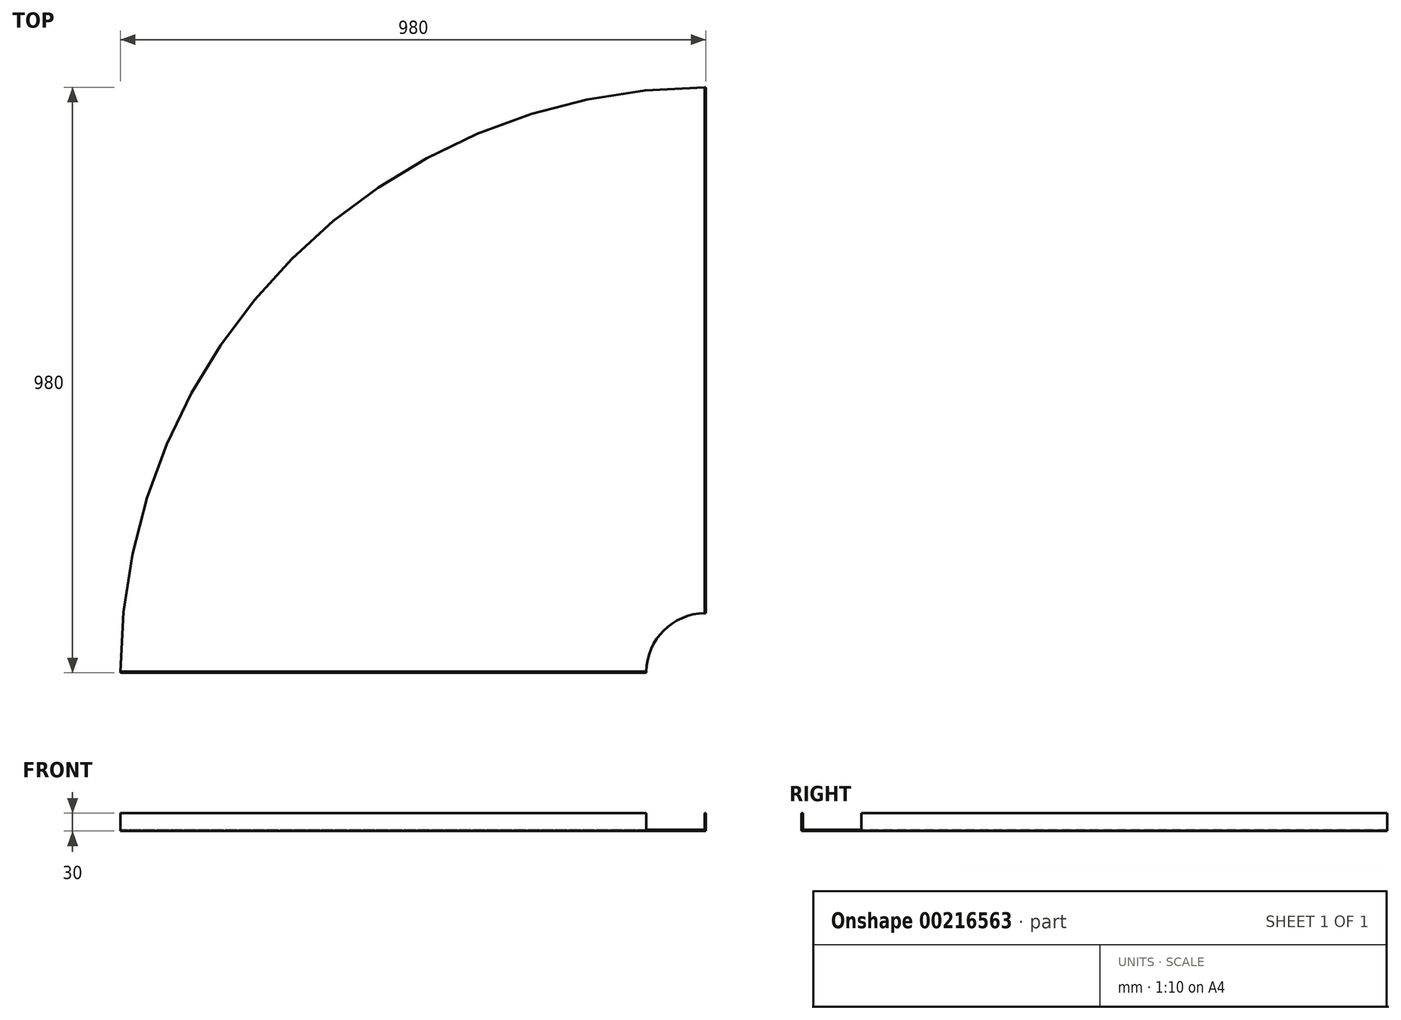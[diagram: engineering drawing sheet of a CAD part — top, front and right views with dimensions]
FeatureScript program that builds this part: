
annotation { "Feature Type Name" : "Feature", "Feature Type Description" : "" }
export const myFeature = defineFeature(function(context is Context, id is Id, definition is map)
    precondition{}
    {
        {
            var Q0;
            Q0=qCreatedBy(makeId("Top.planeOp"),FACE);
            var sketch = newSketch(context, id + "F0", { "sketchPlane" : qUnion([Q0])});
            skArc(sketch, "E0", {"start": v(-2, 99.98) * mm, "mid": v(-70.71, 70.71) * mm, "end": v(-99.98, 2) * mm});
            skArc(sketch, "E1", {"start": v(-2, 980) * mm, "mid": v(-692.96, 692.96) * mm, "end": v(-980, 2) * mm});
            skLineSegment(sketch, "E2", {"start": v(0, 63.88) * mm, "end": v(0, 980) * mm, "construction": true});
            skLineSegment(sketch, "E3", {"start": v(-76.63, 0) * mm, "end": v(-1226.9, 0) * mm, "construction": true});
            skLineSegment(sketch, "E4", {"start": v(-99.98, 2) * mm, "end": v(-980, 2) * mm});
            skPoint(sketch, "E5", {"position": v(-980, 2) * mm});
            skPoint(sketch, "E6", {"position": v(-99.98, 2) * mm});
            skLineSegment(sketch, "E7", {"start": v(-2, 99.98) * mm, "end": v(-2, 980) * mm});
            skPoint(sketch, "E8", {"position": v(-2, 980) * mm});
            skPoint(sketch, "E9", {"position": v(-2, 99.98) * mm});
            skPoint(sketch, "E10", {"position": v(293.18, 448.53) * mm});
            skSolve(sketch);
        }
        {
            var Q0;
            Q0=qCreatedBy(makeId("Top.planeOp"),FACE);
            var sketch = newSketch(context, id + "F1", { "sketchPlane" : qUnion([Q0])});
            skPoint(sketch, "E11.0", {"position": v(-2, 980) * mm});
            skLineSegment(sketch, "E12.0", {"start": v(-2, 99.98) * mm, "end": v(-2, 980) * mm});
            skPoint(sketch, "E13.0", {"position": v(-2, 99.98) * mm});
            skLineSegment(sketch, "E14", {"start": v(-2, 99.98) * mm, "end": v(0, 99.98) * mm});
            skLineSegment(sketch, "E15", {"start": v(-2, 980) * mm, "end": v(0, 980) * mm});
            skLineSegment(sketch, "E16", {"start": v(0, 980) * mm, "end": v(0, 99.98) * mm});
            skPoint(sketch, "E17.0", {"position": v(-99.98, 2) * mm});
            skPoint(sketch, "E18.0", {"position": v(-980, 2) * mm});
            skLineSegment(sketch, "E19", {"start": v(-99.98, 2) * mm, "end": v(-980, 2) * mm});
            skLineSegment(sketch, "E20", {"start": v(-980, 2) * mm, "end": v(-980, 0) * mm});
            skLineSegment(sketch, "E21", {"start": v(-99.98, 2) * mm, "end": v(-99.98, 0) * mm});
            skLineSegment(sketch, "E22", {"start": v(-99.98, 0) * mm, "end": v(-980, 0) * mm});
            skSolve(sketch);
        }
        {
            var Q0;
            Q0 = qSketchRegion(id + "F0", true);
            extrude(context, id + "F2", {"entities" : qUnion([Q0]), "depth" : 2 * mm});
        }
        {
            var Q0;
            Q0 = qSketchRegion(id + "F1", true);
            extrude(context, id + "F3", {"entities" : qUnion([Q0]), "depth" : 30 * mm});
        }
        {
            var Q0;
            Q0 = qSketchRegion(id + "F1", true);
            extrude(context, id + "F4", {"entities" : qUnion([Q0]), "depth" : 30 * mm});
        }
    });
